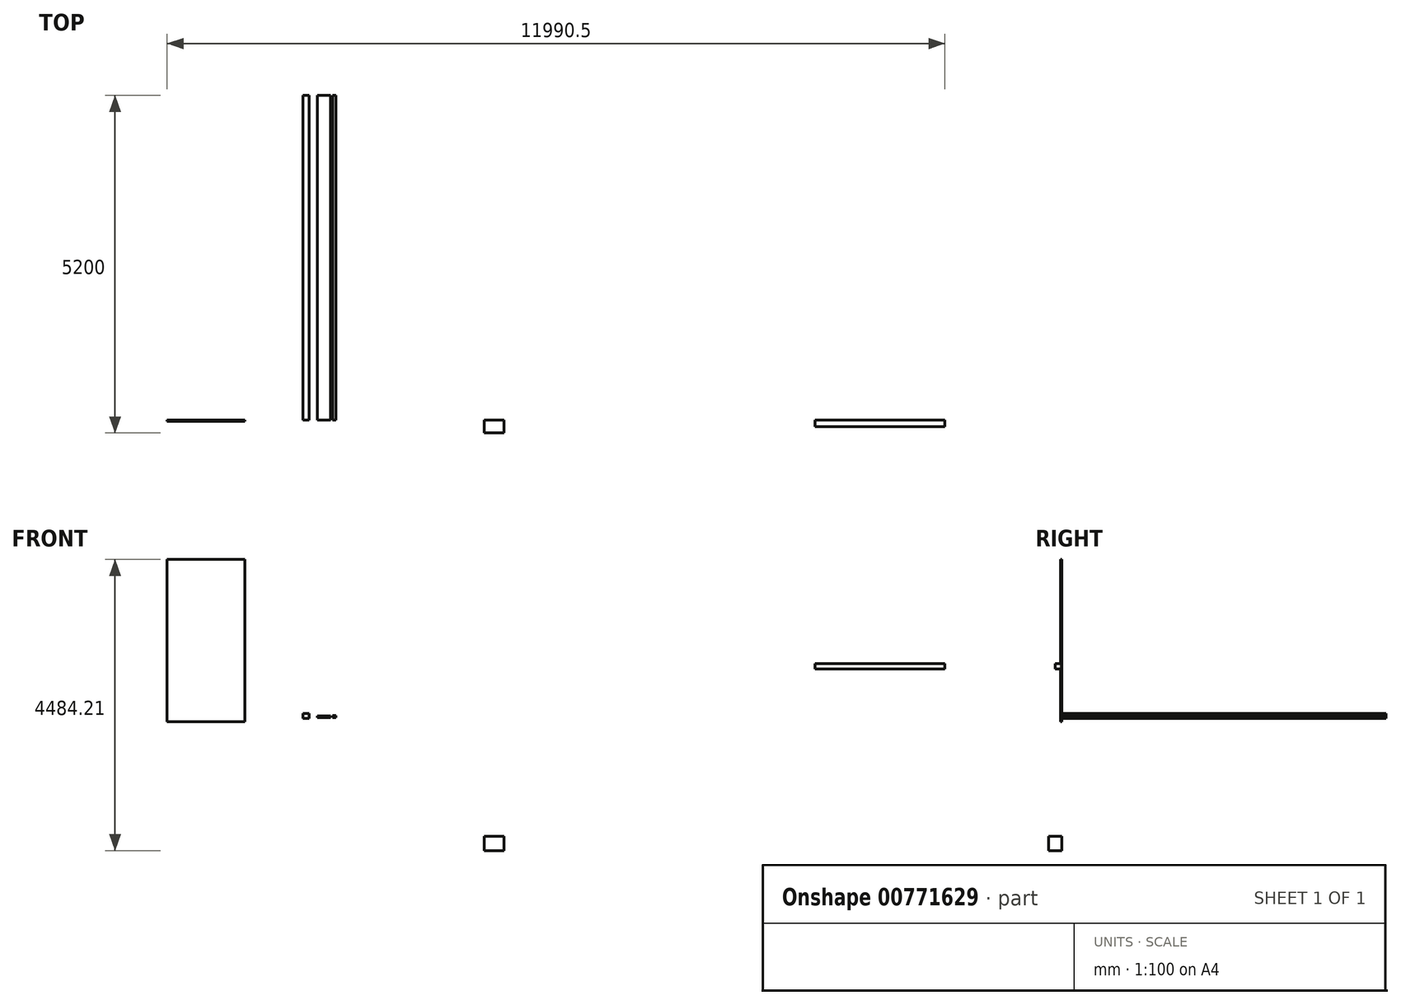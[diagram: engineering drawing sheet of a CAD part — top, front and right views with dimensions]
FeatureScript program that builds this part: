
annotation { "Feature Type Name" : "Feature", "Feature Type Description" : "" }
export const myFeature = defineFeature(function(context is Context, id is Id, definition is map)
    precondition{}
    {
        {
            var Q0;
            Q0=qCreatedBy(makeId("Top.planeOp"),FACE);
            var sketch = newSketch(context, id + "F0", { "sketchPlane" : qUnion([Q0])});
            skLineSegment(sketch, "E0", {"start": v(-2763.67, -3696.1) * mm, "end": v(-2013.67, -3696.1) * mm, "construction": true});
            skLineSegment(sketch, "E1", {"start": v(-2013.67, -3696.1) * mm, "end": v(-2013.67, 1303.9) * mm, "construction": true});
            skLineSegment(sketch, "E2", {"start": v(-2013.67, 1303.9) * mm, "end": v(-2763.67, 1303.9) * mm, "construction": true});
            skLineSegment(sketch, "E3", {"start": v(-2763.67, 1303.9) * mm, "end": v(-2763.67, -3696.1) * mm, "construction": true});
            skLineSegment(sketch, "E4", {"start": v(-2013.67, -3696.1) * mm, "end": v(5986.33, -3696.1) * mm, "construction": true});
            skLineSegment(sketch, "E5", {"start": v(5986.33, -3696.1) * mm, "end": v(5986.33, 1303.9) * mm, "construction": true});
            skLineSegment(sketch, "E6", {"start": v(5986.33, 1303.9) * mm, "end": v(5986.33, 10303.9) * mm, "construction": true});
            skLineSegment(sketch, "E7", {"start": v(5986.33, 10303.9) * mm, "end": v(-271.38, 10303.9) * mm, "construction": true});
            skLineSegment(sketch, "E8", {"start": v(-271.38, 10303.9) * mm, "end": v(-2758.22, 10303.9) * mm, "construction": true});
            skLineSegment(sketch, "E9", {"start": v(-2758.22, 10303.9) * mm, "end": v(-6263.67, 10303.9) * mm, "construction": true});
            skLineSegment(sketch, "E10", {"start": v(-6263.67, 10303.9) * mm, "end": v(-6263.67, 1303.9) * mm, "construction": true});
            skLineSegment(sketch, "E11", {"start": v(-6263.67, 1303.9) * mm, "end": v(-7763.67, -1196.1) * mm, "construction": true});
            skLineSegment(sketch, "E12", {"start": v(-7763.67, -1196.1) * mm, "end": v(-7763.67, -3696.1) * mm, "construction": true});
            skLineSegment(sketch, "E13", {"start": v(-7763.67, -3696.1) * mm, "end": v(-2763.67, -3696.1) * mm, "construction": true});
            skLineSegment(sketch, "E14", {"start": v(-6263.67, 1303.9) * mm, "end": v(-7763.67, 1303.9) * mm, "construction": true});
            skLineSegment(sketch, "E15.bottom", {"start": v(5376.88, -3204.32) * mm, "end": v(-1623.12, -3204.32) * mm});
            skLineSegment(sketch, "E15.top", {"start": v(5376.88, 1795.68) * mm, "end": v(-1623.12, 1795.68) * mm});
            skLineSegment(sketch, "E15.left", {"start": v(5376.88, -3204.32) * mm, "end": v(5376.88, 1795.68) * mm});
            skLineSegment(sketch, "E15.right", {"start": v(-1623.12, -3204.32) * mm, "end": v(-1623.12, 1795.68) * mm});
            skLineSegment(sketch, "E16.bottom", {"start": v(5376.88, 1795.68) * mm, "end": v(4376.88, 1795.68) * mm});
            skLineSegment(sketch, "E16.top", {"start": v(5376.88, 795.68) * mm, "end": v(4376.88, 795.68) * mm});
            skLineSegment(sketch, "E16.left", {"start": v(5376.88, 1795.68) * mm, "end": v(5376.88, 795.68) * mm});
            skLineSegment(sketch, "E16.right", {"start": v(4376.88, 1795.68) * mm, "end": v(4376.88, 795.68) * mm});
            skLineSegment(sketch, "E17.bottom", {"start": v(4218.94, 2394) * mm, "end": v(2218.94, 2394) * mm});
            skLineSegment(sketch, "E17.top", {"start": v(4218.94, 5394) * mm, "end": v(2218.94, 5394) * mm});
            skLineSegment(sketch, "E17.left", {"start": v(4218.94, 2394) * mm, "end": v(4218.94, 5394) * mm});
            skLineSegment(sketch, "E17.right", {"start": v(2218.94, 2394) * mm, "end": v(2218.94, 5394) * mm});
            skSolve(sketch);
        }
        {
            var Q0;
            Q0=qCreatedBy(makeId("Front.planeOp"),FACE);
            var sketch = newSketch(context, id + "F1", { "sketchPlane" : qUnion([Q0])});
            skLineSegment(sketch, "E18", {"start": v(-1623.12, 0) * mm, "end": v(0, 0) * mm, "construction": true});
            skLineSegment(sketch, "E19", {"start": v(0, 0) * mm, "end": v(5376.88, 0) * mm, "construction": true});
            skLineSegment(sketch, "E20.bottom", {"start": v(-1623.12, 0) * mm, "end": v(-1323.12, 0) * mm});
            skLineSegment(sketch, "E20.top", {"start": v(-1623.12, -220) * mm, "end": v(-1323.12, -220) * mm});
            skLineSegment(sketch, "E20.left", {"start": v(-1623.12, 0) * mm, "end": v(-1623.12, -220) * mm});
            skLineSegment(sketch, "E20.right", {"start": v(-1323.12, 0) * mm, "end": v(-1323.12, -220) * mm});
            skLineSegment(sketch, "E21.1.0.0", {"start": v(51.88, 0) * mm, "end": v(351.88, 0) * mm});
            skLineSegment(sketch, "E21.1.0.1", {"start": v(351.88, 0) * mm, "end": v(351.88, -220) * mm});
            skLineSegment(sketch, "E21.1.0.2", {"start": v(51.88, -220) * mm, "end": v(351.88, -220) * mm});
            skLineSegment(sketch, "E21.1.0.3", {"start": v(51.88, 0) * mm, "end": v(51.88, -220) * mm});
            skLineSegment(sketch, "E21.2.0.0", {"start": v(1726.88, 0) * mm, "end": v(2026.88, 0) * mm});
            skLineSegment(sketch, "E21.2.0.1", {"start": v(2026.88, 0) * mm, "end": v(2026.88, -220) * mm});
            skLineSegment(sketch, "E21.2.0.2", {"start": v(1726.88, -220) * mm, "end": v(2026.88, -220) * mm});
            skLineSegment(sketch, "E21.2.0.3", {"start": v(1726.88, 0) * mm, "end": v(1726.88, -220) * mm});
            skLineSegment(sketch, "E21.3.0.0", {"start": v(3401.88, 0) * mm, "end": v(3701.88, 0) * mm});
            skLineSegment(sketch, "E21.3.0.1", {"start": v(3701.88, 0) * mm, "end": v(3701.88, -220) * mm});
            skLineSegment(sketch, "E21.3.0.2", {"start": v(3401.88, -220) * mm, "end": v(3701.88, -220) * mm});
            skLineSegment(sketch, "E21.3.0.3", {"start": v(3401.88, 0) * mm, "end": v(3401.88, -220) * mm});
            skLineSegment(sketch, "E21.4.0.0", {"start": v(5076.88, 0) * mm, "end": v(5376.88, 0) * mm});
            skLineSegment(sketch, "E21.4.0.1", {"start": v(5376.88, 0) * mm, "end": v(5376.88, -220) * mm});
            skLineSegment(sketch, "E21.4.0.2", {"start": v(5076.88, -220) * mm, "end": v(5376.88, -220) * mm});
            skLineSegment(sketch, "E21.4.0.3", {"start": v(5076.88, 0) * mm, "end": v(5076.88, -220) * mm});
            skLineSegment(sketch, "E21.direction1", {"start": v(-1623.12, 0) * mm, "end": v(51.88, 0) * mm, "construction": true});
            skLineSegment(sketch, "E22.bottom", {"start": v(-1523.12, 0) * mm, "end": v(-1423.12, 0) * mm});
            skLineSegment(sketch, "E22.top", {"start": v(-1523.12, 80) * mm, "end": v(-1423.12, 80) * mm});
            skLineSegment(sketch, "E22.left", {"start": v(-1523.12, 0) * mm, "end": v(-1523.12, 80) * mm});
            skLineSegment(sketch, "E22.right", {"start": v(-1423.12, 0) * mm, "end": v(-1423.12, 80) * mm});
            skLineSegment(sketch, "E23", {"start": v(-1473.12, 80) * mm, "end": v(-1473.12, 0) * mm, "construction": true});
            skLineSegment(sketch, "E24.bottom", {"start": v(-1423.12, 80) * mm, "end": v(-1523.12, 80) * mm});
            skLineSegment(sketch, "E24.top", {"start": v(-1423.12, 2580) * mm, "end": v(-1523.12, 2580) * mm});
            skLineSegment(sketch, "E24.left", {"start": v(-1423.12, 80) * mm, "end": v(-1423.12, 2580) * mm});
            skLineSegment(sketch, "E24.right", {"start": v(-1523.12, 80) * mm, "end": v(-1523.12, 2580) * mm});
            skLineSegment(sketch, "E25.bottom", {"start": v(-1523.12, 2580) * mm, "end": v(3476.88, 2580) * mm});
            skLineSegment(sketch, "E25.top", {"start": v(-1523.12, 2660) * mm, "end": v(3476.88, 2660) * mm});
            skLineSegment(sketch, "E25.left", {"start": v(-1523.12, 2580) * mm, "end": v(-1523.12, 2660) * mm});
            skLineSegment(sketch, "E25.right", {"start": v(3476.88, 2580) * mm, "end": v(3476.88, 2660) * mm});
            skLineSegment(sketch, "E26.bottom", {"start": v(3476.88, 2660) * mm, "end": v(5476.88, 2660) * mm});
            skLineSegment(sketch, "E26.top", {"start": v(3476.88, 2580) * mm, "end": v(5476.88, 2580) * mm});
            skLineSegment(sketch, "E26.left", {"start": v(3476.88, 2660) * mm, "end": v(3476.88, 2580) * mm});
            skLineSegment(sketch, "E26.right", {"start": v(5476.88, 2660) * mm, "end": v(5476.88, 2580) * mm});
            skLineSegment(sketch, "E27.bottom", {"start": v(-1523.12, 2660) * mm, "end": v(-1423.12, 2660) * mm});
            skLineSegment(sketch, "E27.top", {"start": v(-1523.12, 2740) * mm, "end": v(-1423.12, 2740) * mm});
            skLineSegment(sketch, "E27.left", {"start": v(-1523.12, 2660) * mm, "end": v(-1523.12, 2740) * mm});
            skLineSegment(sketch, "E27.right", {"start": v(-1423.12, 2660) * mm, "end": v(-1423.12, 2740) * mm});
            skSolve(sketch);
        }
        {
            var Q0;
            Q0=qCreatedBy(makeId("Front.planeOp"),FACE);
            var sketch = newSketch(context, id + "F2", { "sketchPlane" : qUnion([Q0])});
            skLineSegment(sketch, "E28.bottom", {"start": v(-4421.53, 1814.1) * mm, "end": v(-4321.53, 1814.1) * mm});
            skLineSegment(sketch, "E28.top", {"start": v(-4421.53, 1894.1) * mm, "end": v(-4321.53, 1894.1) * mm});
            skLineSegment(sketch, "E28.left", {"start": v(-4421.53, 1814.1) * mm, "end": v(-4421.53, 1894.1) * mm});
            skLineSegment(sketch, "E28.right", {"start": v(-4321.53, 1814.1) * mm, "end": v(-4321.53, 1894.1) * mm});
            skLineSegment(sketch, "E29.bottom", {"start": v(-4195.81, 1826.36) * mm, "end": v(-3995.81, 1826.36) * mm});
            skLineSegment(sketch, "E29.top", {"start": v(-4195.81, 1851.36) * mm, "end": v(-3995.81, 1851.36) * mm});
            skLineSegment(sketch, "E29.left", {"start": v(-4195.81, 1826.36) * mm, "end": v(-4195.81, 1851.36) * mm});
            skLineSegment(sketch, "E29.right", {"start": v(-3995.81, 1826.36) * mm, "end": v(-3995.81, 1851.36) * mm});
            skLineSegment(sketch, "E30.bottom", {"start": v(-3961.53, 1829.43) * mm, "end": v(-3911.53, 1829.43) * mm});
            skLineSegment(sketch, "E30.top", {"start": v(-3961.53, 1859.43) * mm, "end": v(-3911.53, 1859.43) * mm});
            skLineSegment(sketch, "E30.left", {"start": v(-3961.53, 1829.43) * mm, "end": v(-3961.53, 1859.43) * mm});
            skLineSegment(sketch, "E30.right", {"start": v(-3911.53, 1829.43) * mm, "end": v(-3911.53, 1859.43) * mm});
            skLineSegment(sketch, "E31.bottom", {"start": v(-5313.63, 1764.2) * mm, "end": v(-6513.63, 1764.2) * mm});
            skLineSegment(sketch, "E31.top", {"start": v(-5313.63, 4264.2) * mm, "end": v(-6513.63, 4264.2) * mm});
            skLineSegment(sketch, "E31.left", {"start": v(-5313.63, 1764.2) * mm, "end": v(-5313.63, 4264.2) * mm});
            skLineSegment(sketch, "E31.right", {"start": v(-6513.63, 1764.2) * mm, "end": v(-6513.63, 4264.2) * mm});
            skSolve(sketch);
        }
        {
            var Q0;
            Q0=makeQuery(id+"F2.imprint","IMPRINT",FACE,{"disambiguationData":[TD([[makeQuery(id+"F2.imprint","IMPRINT",EDGE,{"derivedFrom":sQuery(id+"F2.wireOp",EDGE,"E28.bottom")}),1.0]])]});
            var Q1;
            Q1=makeQuery(id+"F2.imprint","IMPRINT",FACE,{"disambiguationData":[TD([[makeQuery(id+"F2.imprint","IMPRINT",EDGE,{"derivedFrom":sQuery(id+"F2.wireOp",EDGE,"E29.bottom")}),1.0]])]});
            var Q2;
            Q2=makeQuery(id+"F2.imprint","IMPRINT",FACE,{"disambiguationData":[TD([[makeQuery(id+"F2.imprint","IMPRINT",EDGE,{"derivedFrom":sQuery(id+"F2.wireOp",EDGE,"E30.bottom")}),1.0]])]});
            extrude(context, id + "F3", {"entities" : qUnion([Q0, Q1, Q2]), "oppositeDirection" : true, "depth" : 5000 * mm, "offsetDistance" : 25 * mm});
        }
        {
            var Q0;
            Q0=makeQuery(id+"F1.imprint","IMPRINT",FACE,{"disambiguationData":[TD([[makeQuery(id+"F1.imprint","IMPRINT",EDGE,{"derivedFrom":sQuery(id+"F1.wireOp",EDGE,"E25.right")}),-1.0]])]});
            extrude(context, id + "F4", {"entities" : qUnion([Q0]), "depth" : 100 * mm, "offsetDistance" : 25 * mm});
        }
        {
            var Q0;
            Q0=makeQuery(id+"F1.imprint","IMPRINT",FACE,{"disambiguationData":[TD([[makeQuery(id+"F1.imprint","IMPRINT",EDGE,{"derivedFrom":sQuery(id+"F1.wireOp",EDGE,"E20.top")}),1.0]])]});
            extrude(context, id + "F5", {"entities" : qUnion([Q0]), "depth" : 200 * mm, "offsetDistance" : 25 * mm});
        }
        {
            var Q0;
            Q0=makeQuery(id+"F2.imprint","IMPRINT",FACE,{"disambiguationData":[TD([[makeQuery(id+"F2.imprint","IMPRINT",EDGE,{"derivedFrom":sQuery(id+"F2.wireOp",EDGE,"E31.bottom")}),-1.0]])]});
            extrude(context, id + "F6", {"entities" : qUnion([Q0]), "depth" : 20 * mm, "offsetDistance" : 25 * mm});
        }
    });
